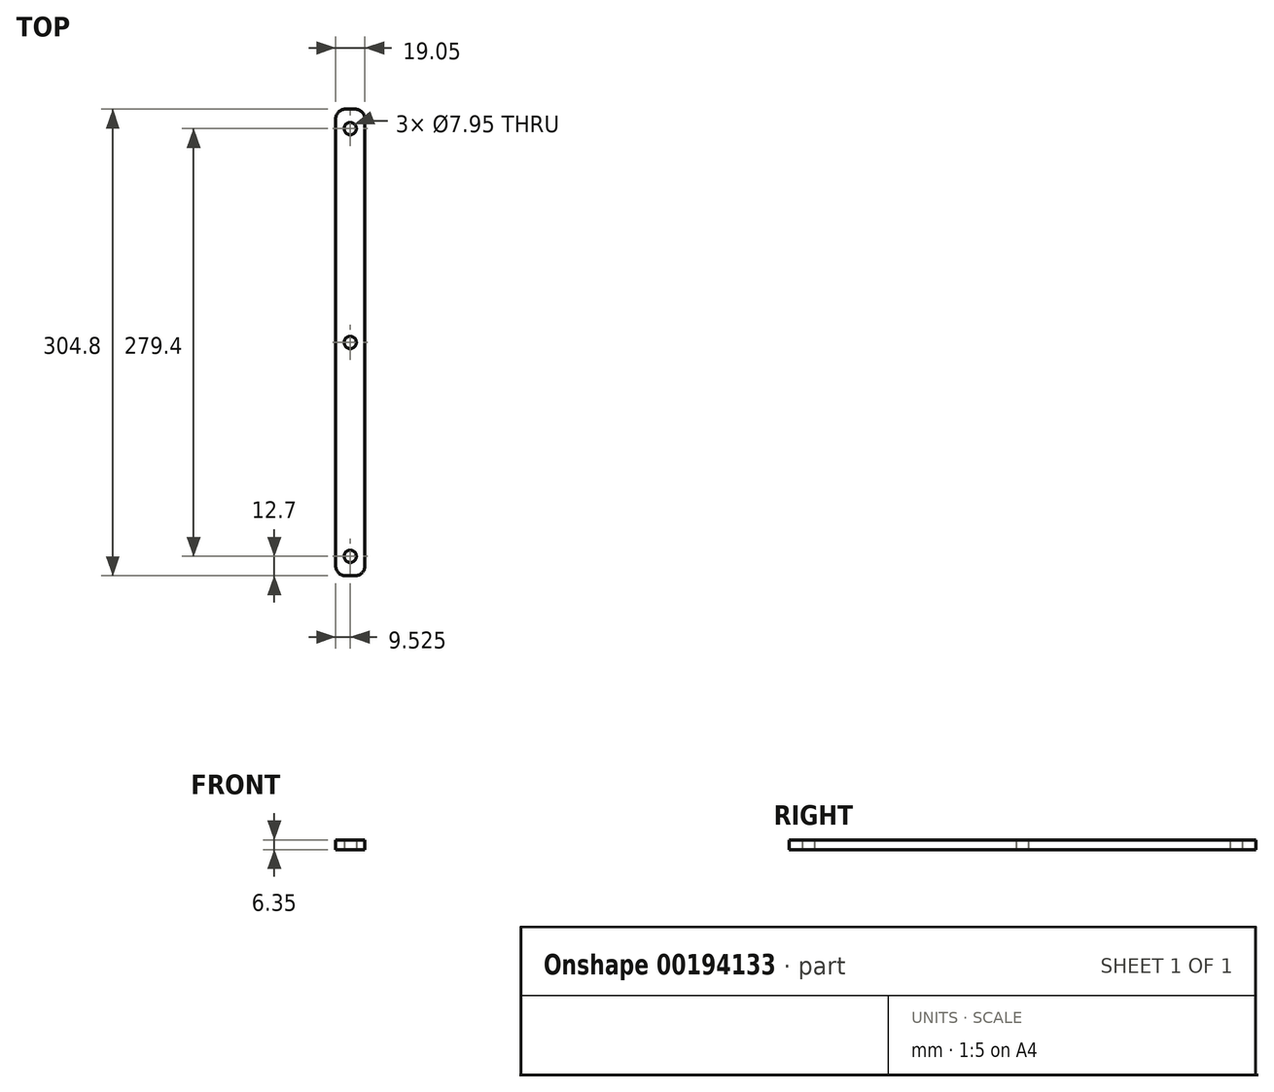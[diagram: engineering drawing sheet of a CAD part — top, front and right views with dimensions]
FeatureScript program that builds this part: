
annotation { "Feature Type Name" : "Feature", "Feature Type Description" : "" }
export const myFeature = defineFeature(function(context is Context, id is Id, definition is map)
    precondition{}
    {
        {
            var Q0;
            Q0=qCreatedBy(makeId("Top.planeOp"),FACE);
            var sketch = newSketch(context, id + "F0", { "sketchPlane" : qUnion([Q0])});
            skLineSegment(sketch, "E0.bottom", {"start": v(6.35, 0) * mm, "end": v(12.7, 0) * mm});
            skLineSegment(sketch, "E0.top", {"start": v(6.35, 304.8) * mm, "end": v(12.7, 304.8) * mm});
            skLineSegment(sketch, "E0.left", {"start": v(0, 6.35) * mm, "end": v(0, 298.45) * mm});
            skLineSegment(sketch, "E0.right", {"start": v(19.05, 6.35) * mm, "end": v(19.05, 298.45) * mm});
            skCircle(sketch, "E1", {"center": v(9.53, 12.7) * mm, "radius": 3.98 * mm});
            skPoint(sketch, "E1.centerSnap0", {"position": v(9.53, 0) * mm});
            skLineSegment(sketch, "E2", {"start": v(0, 152.4) * mm, "end": v(19.05, 152.4) * mm, "construction": true});
            skCircle(sketch, "E3.MirrorC", {"center": v(9.53, 292.1) * mm, "radius": 3.98 * mm});
            skPoint(sketch, "E4.visualSharp", {"position": v(0, 304.8) * mm});
            skArc(sketch, "E4.filletArc", {"start": v(6.35, 304.8) * mm, "mid": v(1.86, 302.94) * mm, "end": v(0, 298.45) * mm});
            skPoint(sketch, "E5.visualSharp", {"position": v(19.05, 304.8) * mm});
            skArc(sketch, "E5.filletArc", {"start": v(19.05, 298.45) * mm, "mid": v(17.2, 302.94) * mm, "end": v(12.7, 304.8) * mm});
            skPoint(sketch, "E6.visualSharp", {"position": v(0, 0) * mm});
            skArc(sketch, "E6.filletArc", {"start": v(0, 6.35) * mm, "mid": v(1.86, 1.86) * mm, "end": v(6.35, 0) * mm});
            skPoint(sketch, "E7.visualSharp", {"position": v(19.05, 0) * mm});
            skArc(sketch, "E7.filletArc", {"start": v(12.7, 0) * mm, "mid": v(17.2, 1.86) * mm, "end": v(19.05, 6.35) * mm});
            skCircle(sketch, "E8", {"center": v(9.53, 152.4) * mm, "radius": 3.98 * mm});
            skSolve(sketch);
        }
        {
            var Q0;
            Q0=makeQuery(id+"F0.imprint","IMPRINT",FACE,{"disambiguationData":[TD([[makeQuery(id+"F0.imprint","IMPRINT",EDGE,{"derivedFrom":sQuery(id+"F0.wireOp",EDGE,"E0.bottom")}),1.0]])]});
            extrude(context, id + "F1", {"entities" : qUnion([Q0]), "depth" : 6.35 * mm});
        }
    });
